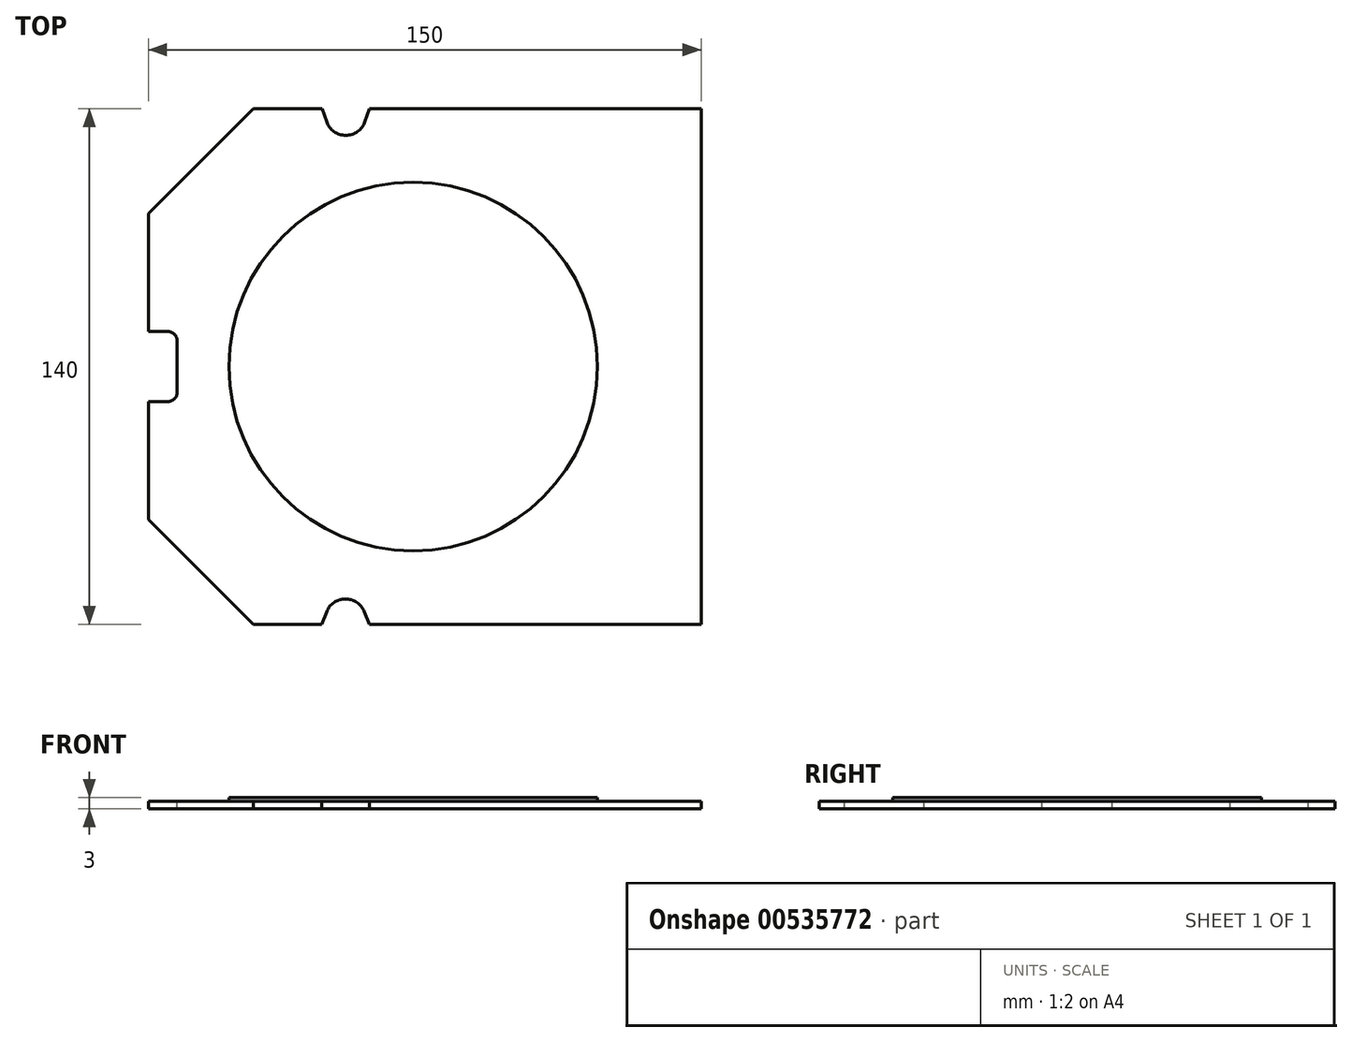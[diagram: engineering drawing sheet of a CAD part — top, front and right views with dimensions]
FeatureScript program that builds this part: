
annotation { "Feature Type Name" : "Feature", "Feature Type Description" : "" }
export const myFeature = defineFeature(function(context is Context, id is Id, definition is map)
    precondition{}
    {
        {
            var Q0;
            Q0=qCreatedBy(makeId("Top.planeOp"),FACE);
            var sketch = newSketch(context, id + "F0", { "sketchPlane" : qUnion([Q0])});
            skLineSegment(sketch, "E0.bottom", {"start": v(75, -70) * mm, "end": v(-75, -70) * mm});
            skLineSegment(sketch, "E0.top", {"start": v(75, 70) * mm, "end": v(-75, 70) * mm});
            skLineSegment(sketch, "E0.left", {"start": v(75, -70) * mm, "end": v(75, 70) * mm});
            skLineSegment(sketch, "E0.right", {"start": v(-75, -70) * mm, "end": v(-75, 70) * mm});
            skPoint(sketch, "E0.middle", {"position": v(0, 0) * mm});
            skSolve(sketch);
        }
        {
            var Q0;
            Q0 = qSketchRegion(id + "F0", true);
            extrude(context, id + "F1", {"entities" : qUnion([Q0]), "depth" : 2 * mm, "offsetDistance" : 25 * mm});
        }
        {
            var Q0;
            Q0=makeQuery(id+"F1.opExtrude","CAP_FACE",FACE,{"disambiguationData":[OSD([sQuery(id+"F0.wireOp",EDGE,"E0.bottom"),sQuery(id+"F0.wireOp",EDGE,"E0.top"),sQuery(id+"F0.wireOp",EDGE,"E0.left"),sQuery(id+"F0.wireOp",EDGE,"E0.right")])],"isStart":false});
            var sketch = newSketch(context, id + "F2", { "sketchPlane" : qUnion([Q0])});
            skLineSegment(sketch, "E1", {"start": v(-75, 41.5) * mm, "end": v(-46.5, 70) * mm});
            skLineSegment(sketch, "E2", {"start": v(-75, -41.5) * mm, "end": v(-46.5, -70) * mm});
            skSolve(sketch);
        }
        {
            var Q0;
            Q0 = qSketchRegion(id + "F2", true);
            var Q1;
            {var subQ0=sQuery(id+"F2.wireOp",EDGE,"E1");Q1=makeQuery(id+"F2.imprint","IMPRINT",FACE,{"disambiguationData":[TD([[makeQuery(id+"F2.imprint","IMPRINT",EDGE,{"derivedFrom":subQ0}),1.0]])]});}
            var Q2;
            {var subQ0=sQuery(id+"F2.wireOp",EDGE,"E2");Q2=makeQuery(id+"F2.imprint","IMPRINT",FACE,{"disambiguationData":[TD([[makeQuery(id+"F2.imprint","IMPRINT",EDGE,{"derivedFrom":subQ0}),-1.0]])]});}
            extrude(context, id + "F3", {"entities" : qUnion([Q0, Q1, Q2]), "operationType" : NewBodyOperationType.REMOVE, "endBound" : BoundingType.THROUGH_ALL, "oppositeDirection" : true, "depth" : 25 * mm, "offsetDistance" : 25 * mm});
        }
        {
            var Q0;
            Q0=makeQuery(id+"F1.opExtrude","CAP_FACE",FACE,{"disambiguationData":[OSD([sQuery(id+"F0.wireOp",EDGE,"E0.bottom"),sQuery(id+"F0.wireOp",EDGE,"E0.top"),sQuery(id+"F0.wireOp",EDGE,"E0.left"),sQuery(id+"F0.wireOp",EDGE,"E0.right")])],"isStart":false});
            var sketch = newSketch(context, id + "F4", { "sketchPlane" : qUnion([Q0])});
            skLineSegment(sketch, "E3", {"start": v(-75, 9.5) * mm, "end": v(-69.68, 9.5) * mm});
            skLineSegment(sketch, "E4", {"start": v(-67.18, 7) * mm, "end": v(-67.18, -7) * mm});
            skArc(sketch, "E5", {"start": v(-67.18, 7) * mm, "mid": v(-67.91, 8.77) * mm, "end": v(-69.68, 9.5) * mm});
            skLineSegment(sketch, "E6", {"start": v(-75, -9.5) * mm, "end": v(-69.68, -9.5) * mm});
            skArc(sketch, "E7", {"start": v(-69.68, -9.5) * mm, "mid": v(-67.91, -8.77) * mm, "end": v(-67.18, -7) * mm});
            skSolve(sketch);
        }
        {
            var Q0;
            Q0 = qSketchRegion(id + "F4", true);
            var Q1;
            {var subQ1=sQuery(id+"F4.wireOp",EDGE,"E3");Q1=makeQuery(id+"F4.imprint","IMPRINT",FACE,{"disambiguationData":[TD([[makeQuery(id+"F4.imprint","IMPRINT",EDGE,{"derivedFrom":subQ1}),-1.0]])]});}
            extrude(context, id + "F5", {"entities" : qUnion([Q0, Q1]), "operationType" : NewBodyOperationType.REMOVE, "endBound" : BoundingType.THROUGH_ALL, "oppositeDirection" : true, "depth" : 25 * mm, "offsetDistance" : 25 * mm});
        }
        {
            var Q0;
            Q0=makeQuery(id+"F1.opExtrude","CAP_FACE",FACE,{"disambiguationData":[OSD([sQuery(id+"F0.wireOp",EDGE,"E0.bottom"),sQuery(id+"F0.wireOp",EDGE,"E0.top"),sQuery(id+"F0.wireOp",EDGE,"E0.left"),sQuery(id+"F0.wireOp",EDGE,"E0.right")])],"isStart":false});
            var sketch = newSketch(context, id + "F6", { "sketchPlane" : qUnion([Q0])});
            skArc(sketch, "E8", {"start": v(-26.63, 66.43) * mm, "mid": v(-21.44, 62.74) * mm, "end": v(-16.24, 66.43) * mm});
            skArc(sketch, "E9", {"start": v(-16.42, -66.5) * mm, "mid": v(-21.52, -63.06) * mm, "end": v(-26.61, -66.5) * mm});
            skLineSegment(sketch, "E10", {"start": v(-27.88, 70) * mm, "end": v(-26.63, 66.43) * mm});
            skLineSegment(sketch, "E11", {"start": v(-15, 70) * mm, "end": v(-16.24, 66.43) * mm});
            skLineSegment(sketch, "E12", {"start": v(-26.61, -66.5) * mm, "end": v(-28.03, -70) * mm});
            skLineSegment(sketch, "E13", {"start": v(-16.42, -66.5) * mm, "end": v(-15, -70) * mm});
            skSolve(sketch);
        }
        {
            var Q0;
            Q0 = qSketchRegion(id + "F6", true);
            var Q1;
            Q1=makeQuery(id+"F6.imprint","IMPRINT",FACE,{"disambiguationData":[TD([[makeQuery(id+"F6.imprint","IMPRINT",EDGE,{"derivedFrom":sQuery(id+"F6.wireOp",EDGE,"E9")}),1.0]])]});
            var Q2;
            Q2=makeQuery(id+"F6.imprint","IMPRINT",FACE,{"disambiguationData":[TD([[makeQuery(id+"F6.imprint","IMPRINT",EDGE,{"derivedFrom":sQuery(id+"F6.wireOp",EDGE,"E8")}),1.0]])]});
            extrude(context, id + "F7", {"entities" : qUnion([Q0, Q1, Q2]), "operationType" : NewBodyOperationType.REMOVE, "endBound" : BoundingType.THROUGH_ALL, "oppositeDirection" : true, "depth" : 25 * mm, "offsetDistance" : 25 * mm});
        }
        {
            var Q0;
            Q0=makeQuery(id+"F1.opExtrude","CAP_FACE",FACE,{"disambiguationData":[OSD([sQuery(id+"F0.wireOp",EDGE,"E0.bottom"),sQuery(id+"F0.wireOp",EDGE,"E0.top"),sQuery(id+"F0.wireOp",EDGE,"E0.left"),sQuery(id+"F0.wireOp",EDGE,"E0.right")])],"isStart":false});
            var sketch = newSketch(context, id + "F8", { "sketchPlane" : qUnion([Q0])});
            skCircle(sketch, "E14", {"center": v(-3.16, 0) * mm, "radius": 50 * mm});
            skPoint(sketch, "E14.first.point", {"position": v(-36.36, 37.39) * mm});
            skPoint(sketch, "E14.second.point", {"position": v(32.35, -35.2) * mm});
            skPoint(sketch, "E14.third.point", {"position": v(42.82, 19.64) * mm});
            skSolve(sketch);
        }
        {
            var Q0;
            Q0 = qSketchRegion(id + "F8", true);
            extrude(context, id + "F9", {"entities" : qUnion([Q0]), "operationType" : NewBodyOperationType.ADD, "depth" : 1 * mm, "offsetDistance" : 25 * mm});
        }
    });
